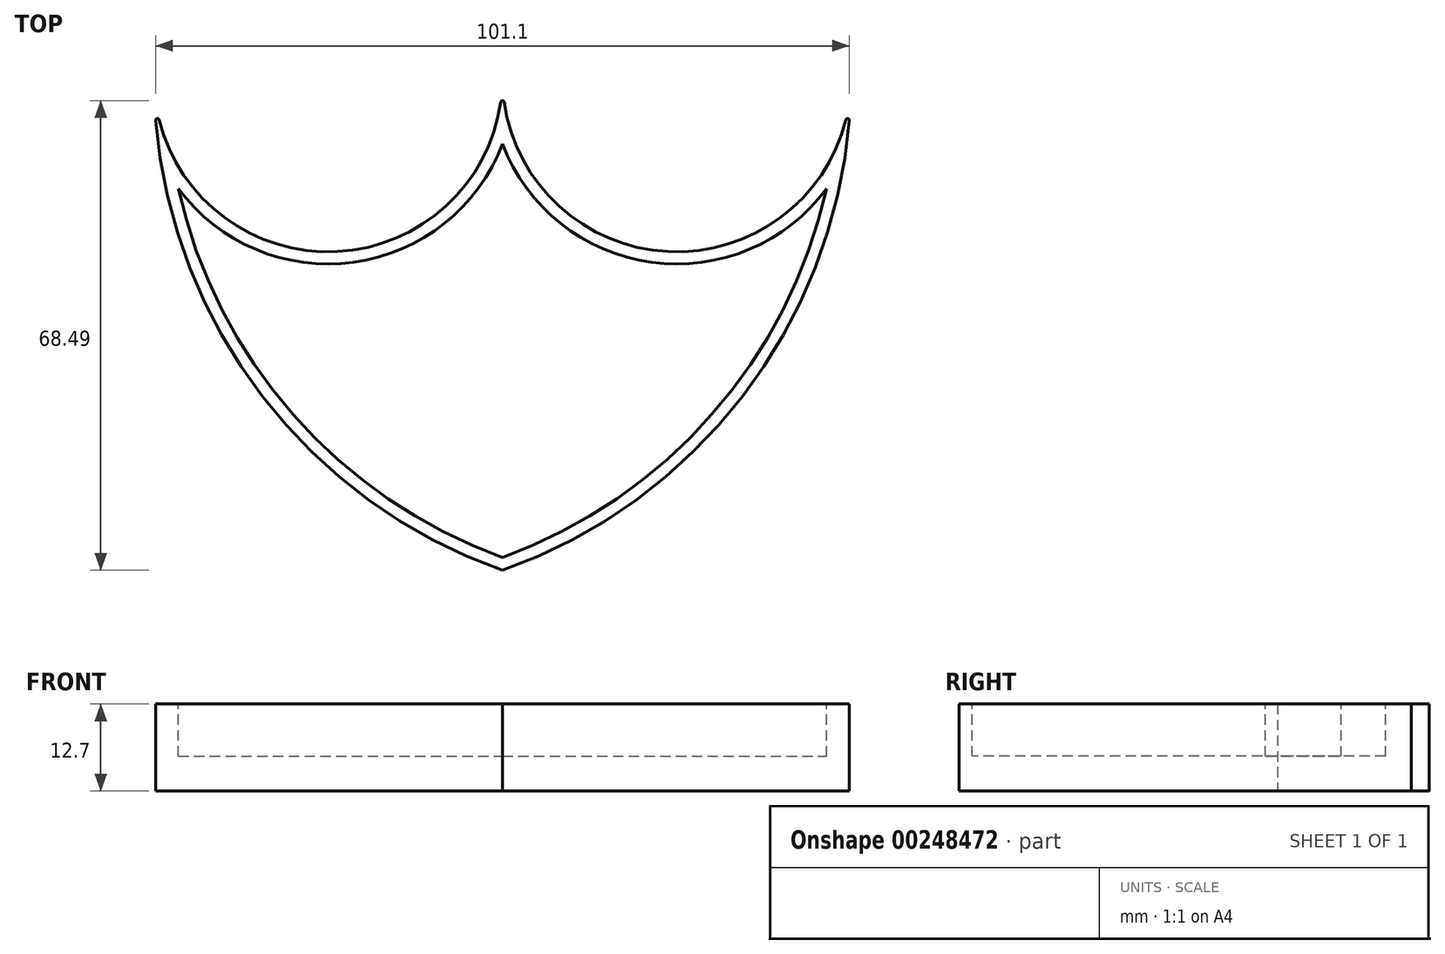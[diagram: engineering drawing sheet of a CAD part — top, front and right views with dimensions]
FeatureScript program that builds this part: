
annotation { "Feature Type Name" : "Feature", "Feature Type Description" : "" }
export const myFeature = defineFeature(function(context is Context, id is Id, definition is map)
    precondition{}
    {
        {
            var Q0;
            Q0=qCreatedBy(makeId("Top.planeOp"),FACE);
            var sketch = newSketch(context, id + "F0", { "sketchPlane" : qUnion([Q0])});
            skLineSegment(sketch, "E0", {"start": v(0, 0) * mm, "end": v(50.8, 0) * mm, "construction": true});
            skLineSegment(sketch, "E1", {"start": v(0, 0) * mm, "end": v(-50.8, 0) * mm, "construction": true});
            skPoint(sketch, "E1.endSnap0", {"position": v(25.4, 0) * mm});
            skArc(sketch, "E2", {"start": v(-50.05, -6.14) * mm, "mid": v(-24.09, -25.37) * mm, "end": v(-0.25, -3.57) * mm});
            skLineSegment(sketch, "E3", {"start": v(0, 0) * mm, "end": v(0, -76.2) * mm, "construction": true});
            skArc(sketch, "E4", {"start": v(-50.55, -6.23) * mm, "mid": v(-34.97, -46.5) * mm, "end": v(0, -71.84) * mm});
            skArc(sketch, "E5", {"start": v(50.55, -6.23) * mm, "mid": v(34.97, -46.5) * mm, "end": v(0, -71.84) * mm});
            skArc(sketch, "E6", {"start": v(0.25, -3.57) * mm, "mid": v(24.09, -25.37) * mm, "end": v(50.05, -6.14) * mm});
            skPoint(sketch, "E7.visualSharp", {"position": v(-50.8, 0) * mm});
            skArc(sketch, "E7.filletArc", {"start": v(-50.05, -6.14) * mm, "mid": v(-50.33, -5.96) * mm, "end": v(-50.55, -6.23) * mm});
            skPoint(sketch, "E8.visualSharp", {"position": v(50.8, 0) * mm});
            skArc(sketch, "E8.filletArc", {"start": v(50.55, -6.23) * mm, "mid": v(50.33, -5.96) * mm, "end": v(50.05, -6.14) * mm});
            skPoint(sketch, "E9.visualSharp", {"position": v(0, 0) * mm});
            skArc(sketch, "E9.filletArc", {"start": v(0.25, -3.57) * mm, "mid": v(0, -3.35) * mm, "end": v(-0.25, -3.57) * mm});
            skSolve(sketch);
        }
        {
            var Q0;
            Q0=makeQuery(id+"F0.imprint","IMPRINT",FACE,{"disambiguationData":[TD([[makeQuery(id+"F0.imprint","IMPRINT",EDGE,{"derivedFrom":sQuery(id+"F0.wireOp",EDGE,"E2")}),-1.0]])]});
            extrude(context, id + "F1", {"entities" : qUnion([Q0]), "depth" : 12.7 * mm});
        }
        {
            var Q0;
            Q0=makeQuery(id+"F1.opExtrude","CAP_FACE",FACE,{"disambiguationData":[OSD([sQuery(id+"F0.wireOp",EDGE,"E2"),sQuery(id+"F0.wireOp",EDGE,"E4"),sQuery(id+"F0.wireOp",EDGE,"E5"),sQuery(id+"F0.wireOp",EDGE,"E6"),sQuery(id+"F0.wireOp",EDGE,"E7.filletArc"),sQuery(id+"F0.wireOp",EDGE,"E8.filletArc"),sQuery(id+"F0.wireOp",EDGE,"E9.filletArc")])],"isStart":false});
            var sketch = newSketch(context, id + "F2", { "sketchPlane" : qUnion([Q0])});
            skArc(sketch, "E10.0", {"start": v(0, -69.95) * mm, "mid": v(30.51, -49.12) * mm, "end": v(47.24, -16.17) * mm});
            skArc(sketch, "E10.1", {"start": v(-47.24, -16.17) * mm, "mid": v(-30.51, -49.12) * mm, "end": v(0, -69.95) * mm});
            skArc(sketch, "E10.2", {"start": v(0, -9.67) * mm, "mid": v(-21.7, -26.92) * mm, "end": v(-47.24, -16.17) * mm});
            skArc(sketch, "E10.3", {"start": v(47.24, -16.17) * mm, "mid": v(21.7, -26.92) * mm, "end": v(0, -9.67) * mm});
            skSolve(sketch);
        }
        {
            var Q0;
            Q0=makeQuery(id+"F2.imprint","IMPRINT",FACE,{"disambiguationData":[TD([[makeQuery(id+"F2.imprint","IMPRINT",EDGE,{"derivedFrom":sQuery(id+"F2.wireOp",EDGE,"E10.0")}),1.0]])]});
            extrude(context, id + "F3", {"entities" : qUnion([Q0]), "operationType" : NewBodyOperationType.REMOVE, "oppositeDirection" : true, "depth" : 7.62 * mm});
        }
    });
